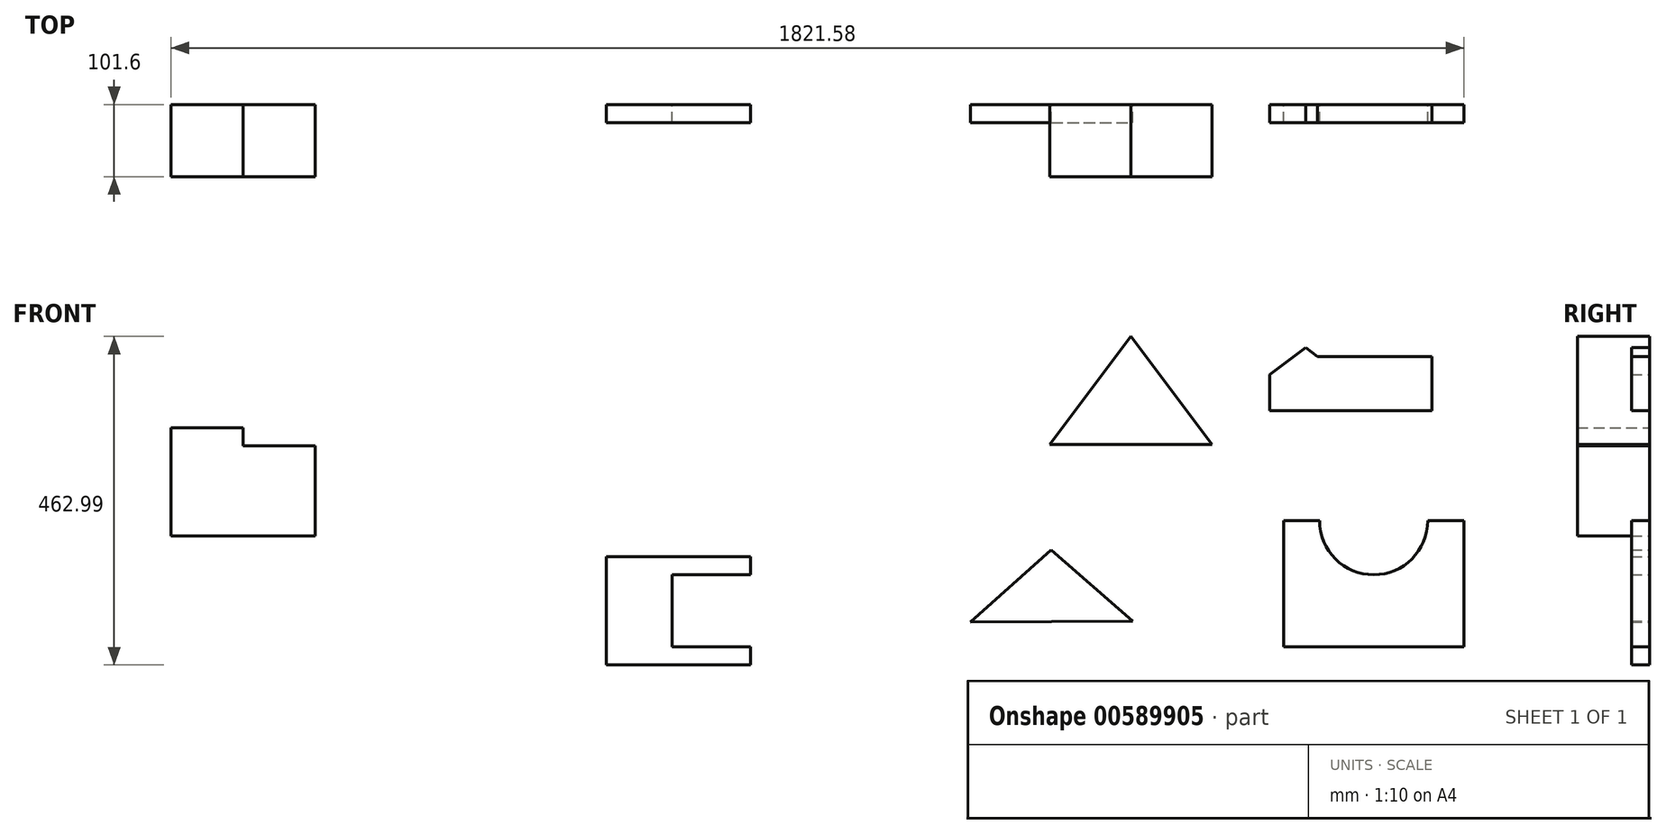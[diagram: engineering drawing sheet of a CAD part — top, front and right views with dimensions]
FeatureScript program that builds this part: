
annotation { "Feature Type Name" : "Feature", "Feature Type Description" : "" }
export const myFeature = defineFeature(function(context is Context, id is Id, definition is map)
    precondition{}
    {
        {
            var Q0;
            Q0=qCreatedBy(makeId("Front.planeOp"),FACE);
            var sketch = newSketch(context, id + "F0", { "sketchPlane" : qUnion([Q0])});
            skLineSegment(sketch, "E0", {"start": v(279.13, -60.55) * mm, "end": v(507.73, -60.55) * mm});
            skLineSegment(sketch, "E1", {"start": v(279.13, -60.55) * mm, "end": v(393.43, 91.85) * mm});
            skLineSegment(sketch, "E2", {"start": v(393.43, 91.85) * mm, "end": v(507.73, -60.55) * mm});
            skLineSegment(sketch, "E3", {"start": v(336.28, 15.65) * mm, "end": v(450.58, 15.65) * mm});
            skSolve(sketch);
        }
        {
            var Q0;
            Q0 = qSketchRegion(id + "F0", true);
            extrude(context, id + "F1", {"entities" : qUnion([Q0]), "depth" : 101.6 * mm, "offsetDistance" : 25.4 * mm});
        }
        {
            var Q0;
            Q0=qCreatedBy(makeId("Front.planeOp"),FACE);
            var sketch = newSketch(context, id + "F2", { "sketchPlane" : qUnion([Q0])});
            skLineSegment(sketch, "E4", {"start": v(817.2, -12.67) * mm, "end": v(817.2, 38.13) * mm});
            skLineSegment(sketch, "E5", {"start": v(817.2, 38.13) * mm, "end": v(690.2, 38.13) * mm});
            skLineSegment(sketch, "E6", {"start": v(690.2, 38.13) * mm, "end": v(690.2, -12.67) * mm});
            skLineSegment(sketch, "E7", {"start": v(690.2, -12.67) * mm, "end": v(817.2, -12.67) * mm});
            skLineSegment(sketch, "E8", {"start": v(690.2, 38.13) * mm, "end": v(639.4, 76.23) * mm});
            skLineSegment(sketch, "E9", {"start": v(690.2, -12.67) * mm, "end": v(588.6, -12.67) * mm});
            skLineSegment(sketch, "E10", {"start": v(588.6, -12.67) * mm, "end": v(588.6, 38.13) * mm});
            skLineSegment(sketch, "E11", {"start": v(639.4, 76.23) * mm, "end": v(588.6, 38.13) * mm});
            skLineSegment(sketch, "E12", {"start": v(817.2, 38.13) * mm, "end": v(817.2, 63.53) * mm});
            skLineSegment(sketch, "E13", {"start": v(817.2, 63.53) * mm, "end": v(656.34, 63.53) * mm});
            skSolve(sketch);
        }
        {
            var Q0;
            Q0=qCreatedBy(makeId("Front.planeOp"),FACE);
            var sketch = newSketch(context, id + "F3", { "sketchPlane" : qUnion([Q0])});
            skLineSegment(sketch, "E14", {"start": v(-755.93, -189.66) * mm, "end": v(-755.93, -62.66) * mm});
            skLineSegment(sketch, "E15", {"start": v(-959.13, -189.66) * mm, "end": v(-755.93, -189.66) * mm});
            skLineSegment(sketch, "E16", {"start": v(-755.93, -62.66) * mm, "end": v(-857.53, -62.66) * mm});
            skLineSegment(sketch, "E17", {"start": v(-857.53, -62.66) * mm, "end": v(-857.53, -37.26) * mm});
            skLineSegment(sketch, "E18", {"start": v(-857.53, -37.26) * mm, "end": v(-959.13, -37.26) * mm});
            skLineSegment(sketch, "E19", {"start": v(-959.13, -37.26) * mm, "end": v(-959.13, -189.66) * mm});
            skSolve(sketch);
        }
        {
            var Q0;
            Q0=makeQuery(id+"F3.imprint","IMPRINT",FACE,{"disambiguationData":[TD([[makeQuery(id+"F3.imprint","IMPRINT",EDGE,{"derivedFrom":sQuery(id+"F3.wireOp",EDGE,"E14")}),1.0]])]});
            extrude(context, id + "F4", {"entities" : qUnion([Q0]), "depth" : 101.6 * mm, "offsetDistance" : 25.4 * mm});
        }
        {
            var Q0;
            Q0=qCreatedBy(makeId("Front.planeOp"),FACE);
            var sketch = newSketch(context, id + "F5", { "sketchPlane" : qUnion([Q0])});
            skLineSegment(sketch, "E20", {"start": v(-142.85, -371.14) * mm, "end": v(-142.85, -218.74) * mm});
            skLineSegment(sketch, "E21", {"start": v(-142.85, -218.74) * mm, "end": v(-346.05, -218.74) * mm});
            skLineSegment(sketch, "E22", {"start": v(-346.05, -218.74) * mm, "end": v(-346.05, -371.14) * mm});
            skLineSegment(sketch, "E23", {"start": v(-346.05, -371.14) * mm, "end": v(-142.85, -371.14) * mm});
            skLineSegment(sketch, "E24", {"start": v(-142.85, -244.14) * mm, "end": v(-253.26, -244.14) * mm});
            skLineSegment(sketch, "E25", {"start": v(-253.26, -244.14) * mm, "end": v(-253.26, -345.74) * mm});
            skLineSegment(sketch, "E26", {"start": v(-253.26, -345.74) * mm, "end": v(-142.85, -345.74) * mm});
            skSolve(sketch);
        }
        {
            var Q0;
            {var subQ0=sQuery(id+"F5.wireOp",EDGE,"E21");Q0=makeQuery(id+"F5.imprint","IMPRINT",FACE,{"disambiguationData":[TD([[makeQuery(id+"F5.imprint","IMPRINT",EDGE,{"derivedFrom":subQ0}),1.0]])]});}
            extrude(context, id + "F6", {"entities" : qUnion([Q0]), "depth" : 25.4 * mm, "offsetDistance" : 25.4 * mm});
        }
        {
            var Q0;
            Q0=qCreatedBy(makeId("Front.planeOp"),FACE);
            var sketch = newSketch(context, id + "F7", { "sketchPlane" : qUnion([Q0])});
            skLineSegment(sketch, "E27", {"start": v(862.45, -345.66) * mm, "end": v(862.45, -167.86) * mm});
            skLineSegment(sketch, "E28", {"start": v(862.45, -167.86) * mm, "end": v(608.45, -167.86) * mm});
            skLineSegment(sketch, "E29", {"start": v(608.45, -167.86) * mm, "end": v(608.45, -345.66) * mm});
            skLineSegment(sketch, "E30", {"start": v(608.45, -345.66) * mm, "end": v(862.45, -345.66) * mm});
            skArc(sketch, "E31", {"start": v(659.25, -167.86) * mm, "mid": v(735.45, -244.06) * mm, "end": v(811.65, -167.86) * mm});
            skSolve(sketch);
        }
        {
            var Q0;
            {var subQ3=sQuery(id+"F7.wireOp",EDGE,"E27");Q0=makeQuery(id+"F7.imprint","IMPRINT",FACE,{"disambiguationData":[TD([[makeQuery(id+"F7.imprint","IMPRINT",EDGE,{"derivedFrom":subQ3}),1.0]])]});}
            extrude(context, id + "F8", {"entities" : qUnion([Q0]), "depth" : 25.4 * mm, "offsetDistance" : 25.4 * mm});
        }
        {
            var Q0;
            {var subQ3=sQuery(id+"F2.wireOp",EDGE,"E6");Q0=makeQuery(id+"F2.imprint","IMPRINT",FACE,{"disambiguationData":[TD([[makeQuery(id+"F2.imprint","IMPRINT",EDGE,{"derivedFrom":subQ3}),-1.0]])]});}
            var Q1;
            Q1=makeQuery(id+"F2.imprint","IMPRINT",FACE,{"disambiguationData":[TD([[makeQuery(id+"F2.imprint","IMPRINT",EDGE,{"derivedFrom":sQuery(id+"F2.wireOp",EDGE,"E4")}),1.0]])]});
            var Q2;
            {var subQ0=sQuery(id+"F2.wireOp",EDGE,"E5");Q2=makeQuery(id+"F2.imprint","IMPRINT",FACE,{"disambiguationData":[TD([[makeQuery(id+"F2.imprint","IMPRINT",EDGE,{"derivedFrom":subQ0}),-1.0]])]});}
            extrude(context, id + "F9", {"entities" : qUnion([Q0, Q1, Q2]), "depth" : 25.4 * mm, "offsetDistance" : 25.4 * mm});
        }
        {
            var Q0;
            Q0=qCreatedBy(makeId("Front.planeOp"),FACE);
            var sketch = newSketch(context, id + "F10", { "sketchPlane" : qUnion([Q0])});
            skLineSegment(sketch, "E32", {"start": v(167.14, -310.88) * mm, "end": v(395.73, -309.29) * mm});
            skLineSegment(sketch, "E33", {"start": v(167.14, -310.88) * mm, "end": v(280.73, -209.29) * mm});
            skLineSegment(sketch, "E34", {"start": v(280.73, -209.29) * mm, "end": v(395.73, -309.29) * mm});
            skSolve(sketch);
        }
        {
            var Q0;
            Q0 = qSketchRegion(id + "F10", true);
            extrude(context, id + "F11", {"entities" : qUnion([Q0]), "depth" : 25.4 * mm, "offsetDistance" : 25.4 * mm});
        }
    });
